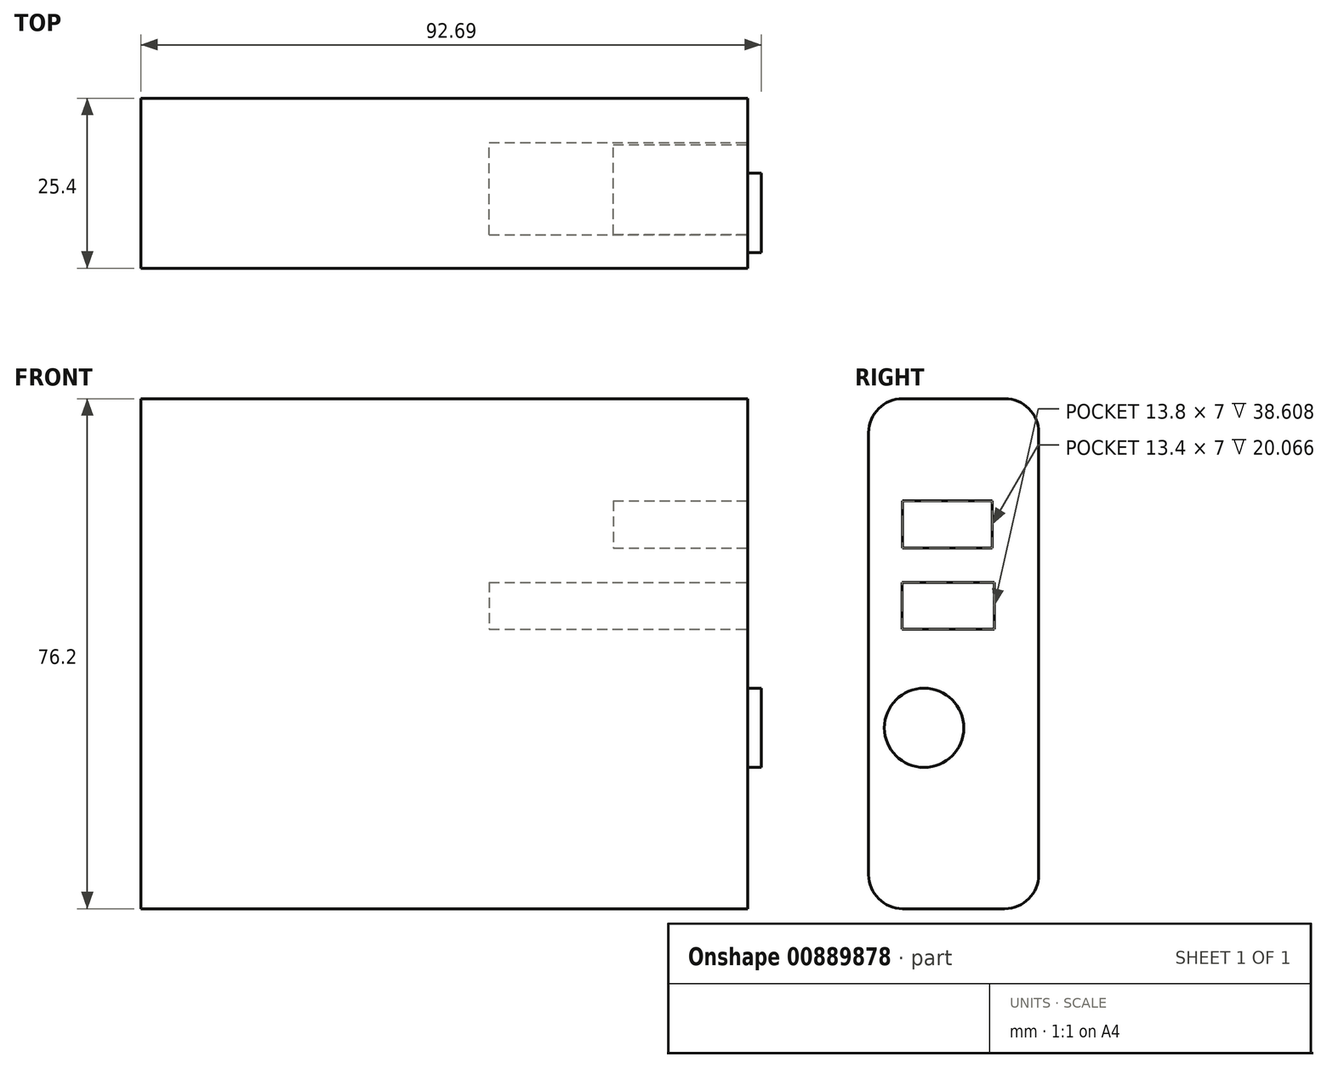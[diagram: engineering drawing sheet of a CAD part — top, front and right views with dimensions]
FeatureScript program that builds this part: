
annotation { "Feature Type Name" : "Feature", "Feature Type Description" : "" }
export const myFeature = defineFeature(function(context is Context, id is Id, definition is map)
    precondition{}
    {
        {
            var Q0;
            Q0=qCreatedBy(makeId("Front.planeOp"),FACE);
            var sketch = newSketch(context, id + "F0", { "sketchPlane" : qUnion([Q0])});
            skLineSegment(sketch, "E0.bottom", {"start": v(-45.33, 38.1) * mm, "end": v(45.33, 38.1) * mm});
            skLineSegment(sketch, "E0.top", {"start": v(-45.33, -38.1) * mm, "end": v(45.33, -38.1) * mm});
            skLineSegment(sketch, "E0.left", {"start": v(-45.33, 38.1) * mm, "end": v(-45.33, -38.1) * mm});
            skLineSegment(sketch, "E0.right", {"start": v(45.33, 38.1) * mm, "end": v(45.33, -38.1) * mm});
            skPoint(sketch, "E0.middle", {"position": v(0, 0) * mm});
            skSolve(sketch);
        }
        {
            var Q0;
            Q0 = qSketchRegion(id + "F0", true);
            extrude(context, id + "F1", {"entities" : qUnion([Q0]), "depth" : 25.4 * mm, "offsetDistance" : 25.4 * mm});
        }
        {
            var Q0;
            Q0=makeQuery(id+"F1.opExtrude","CAP_EDGE",EDGE,{"disambiguationData":[OSD([sQuery(id+"F0.wireOp",EDGE,"E0.bottom")])],"isStart":false});
            var Q1;
            Q1=makeQuery(id+"F1.opExtrude","CAP_EDGE",EDGE,{"disambiguationData":[OSD([sQuery(id+"F0.wireOp",EDGE,"E0.bottom")])],"isStart":true});
            var Q2;
            Q2=makeQuery(id+"F1.opExtrude","CAP_EDGE",EDGE,{"disambiguationData":[OSD([sQuery(id+"F0.wireOp",EDGE,"E0.top")])],"isStart":true});
            var Q3;
            Q3=makeQuery(id+"F1.opExtrude","CAP_EDGE",EDGE,{"disambiguationData":[OSD([sQuery(id+"F0.wireOp",EDGE,"E0.top")])],"isStart":false});
            fillet(context, id + "F2", {"entities" : qUnion([Q0, Q1, Q2, Q3]), "radius" : 5.08 * mm, "tangentPropagation" : true, "allowEdgeOverflow" : false});
        }
        {
            var Q0;
            Q0=makeQuery(id+"F1.opExtrude","SWEPT_FACE",FACE,{"disambiguationData":[OSD([sQuery(id+"F0.wireOp",EDGE,"E0.right")])]});
            var sketch = newSketch(context, id + "F3", { "sketchPlane" : qUnion([Q0])});
            skLineSegment(sketch, "E1.bottom", {"start": v(-20.43, 10.66) * mm, "end": v(-6.63, 10.66) * mm});
            skLineSegment(sketch, "E1.top", {"start": v(-20.43, 3.66) * mm, "end": v(-6.63, 3.66) * mm});
            skLineSegment(sketch, "E1.left", {"start": v(-20.43, 10.66) * mm, "end": v(-20.43, 3.66) * mm});
            skLineSegment(sketch, "E1.right", {"start": v(-6.63, 10.66) * mm, "end": v(-6.63, 3.66) * mm});
            skSolve(sketch);
        }
        {
            var Q0;
            Q0=makeQuery(id+"F3.imprint","IMPRINT",FACE,{"disambiguationData":[TD([[makeQuery(id+"F3.imprint","IMPRINT",EDGE,{"derivedFrom":sQuery(id+"F3.wireOp",EDGE,"E1.bottom")}),-1.0]])]});
            extrude(context, id + "F4", {"entities" : qUnion([Q0]), "operationType" : NewBodyOperationType.REMOVE, "oppositeDirection" : true, "depth" : 38.6 * mm, "offsetDistance" : 25.4 * mm});
        }
        {
            var Q0;
            Q0=makeQuery(id+"F1.opExtrude","SWEPT_FACE",FACE,{"disambiguationData":[OSD([sQuery(id+"F0.wireOp",EDGE,"E0.right")])]});
            var sketch = newSketch(context, id + "F5", { "sketchPlane" : qUnion([Q0])});
            skLineSegment(sketch, "E2.bottom", {"start": v(-20.37, 22.8) * mm, "end": v(-6.97, 22.8) * mm});
            skLineSegment(sketch, "E2.top", {"start": v(-20.37, 15.8) * mm, "end": v(-6.97, 15.8) * mm});
            skLineSegment(sketch, "E2.left", {"start": v(-20.37, 22.8) * mm, "end": v(-20.37, 15.8) * mm});
            skLineSegment(sketch, "E2.right", {"start": v(-6.97, 22.8) * mm, "end": v(-6.97, 15.8) * mm});
            skSolve(sketch);
        }
        {
            var Q0;
            Q0 = qSketchRegion(id + "F5", true);
            extrude(context, id + "F6", {"entities" : qUnion([Q0]), "operationType" : NewBodyOperationType.REMOVE, "oppositeDirection" : true, "depth" : 20.07 * mm, "offsetDistance" : 25.4 * mm});
        }
        {
            var Q0;
            Q0=makeQuery(id+"F1.opExtrude","SWEPT_FACE",FACE,{"disambiguationData":[OSD([sQuery(id+"F0.wireOp",EDGE,"E0.right")])]});
            var sketch = newSketch(context, id + "F7", { "sketchPlane" : qUnion([Q0])});
            skCircle(sketch, "E3", {"center": v(-17.12, -11.08) * mm, "radius": 5.93 * mm});
            skSolve(sketch);
        }
        {
            var Q0;
            Q0 = qSketchRegion(id + "F7", true);
            extrude(context, id + "F8", {"entities" : qUnion([Q0]), "operationType" : NewBodyOperationType.ADD, "depth" : 2.03 * mm, "offsetDistance" : 25.4 * mm});
        }
    });
